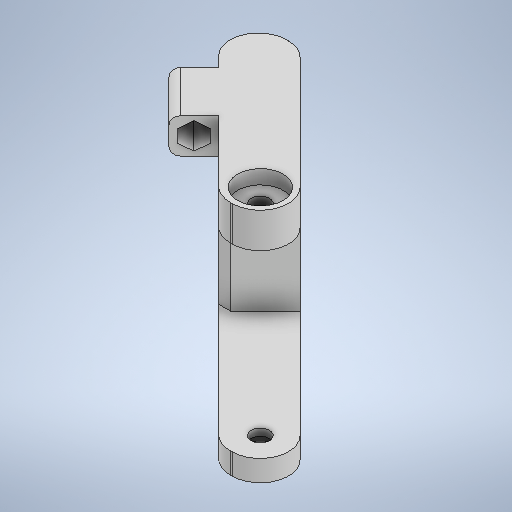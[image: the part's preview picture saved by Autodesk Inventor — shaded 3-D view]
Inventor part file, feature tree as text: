
AUTODESK INVENTOR PART (.ipt)
format: ipt  version: 2025 (Build 290162010, 162A)  size: 349,184 bytes
history: native  units: in
note: dims shown in document units (in); Inventor stores cm internally (conversion verified against a paired STEP export)
features: extrude x7, sketch x7, fillet x2, chamfer x1, projected_geometry x1
ambient origin geometry x8: Origin, YZ Plane, XZ Plane, XY Plane, X Axis, Y Axis, Z Axis, Center Point
bodies: Volumenkörper1 (feature_tree)
feature tree (18):
  extrude  "Extrusion1"  TaperAngle=45.0deg  [1 undecoded]
  fillet  "Rundung2"  Radius=3.3071in
  extrude  "Extrusion18"  Depth=0.3937in
  extrude  "Extrusion19"  Depth=0.1969in TaperAngle=0.0deg
  extrude  "Extrusion20"  Depth=0.1969in
  extrude  "Extrusion21"  Depth=1.1417in
  chamfer  "Fasen4"  Distance=0.2953in
  extrude  "Extrusion22"  Depth=0.1181in
  extrude  "Extrusion23"  Depth=0.1181in
  fillet  "Rundung3"  [1 undecoded]
  sketch  "Skizze1"  dims[d0=3.3465in d1=45.0deg d2=3.3071in d3=0.0in]
  sketch  "Skizze17"  dims[d85=0.6398in d86=0.3937in]
  sketch  "Skizze19"  dims[d87=0.3937in d92=0.1969in d93=0.0in]
  sketch  "Skizze20"  dims[d94=0.1969in d95=0.0in d96=0.2559in]
  sketch  "Skizze21"  dims[d97=0.0in d98=0.0in d99=1.1417in]
  projected_geometry  "Projizierte Kontur1"
  sketch  "Skizze22"  dims[d100=0.3937in]
  sketch  "Skizze23"  dims[d101=0.4921in d102=0.2953in d103=0.1181in d104=2.7559in d105=0.0in d106=0.0in d107=0.1181in d108=0.0787in d109=45.0deg d110=0.8268in d112=0.4921in d113=0.0in d114=0.3189in d115=0.0886in d116=0.0in d117=0.0in d118=0.1969in d119=0.1181in d37=0.0197in d38=0.0344in d39=0.0197in d40=0.0344in d41=0.0197in d42=0.0344in]
note: 2 required parameter values undecoded (feature->parameter linkage not recoverable at this tier; creation-order binding heuristic only, values carry confidence <= 0.55)
